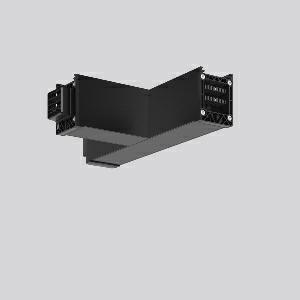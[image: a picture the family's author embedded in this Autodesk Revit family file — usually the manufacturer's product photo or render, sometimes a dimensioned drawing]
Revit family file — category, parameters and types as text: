
# Revit family: linedo_t-verbindung_982774_003_8bc5
name_source: partatom
category: Lighting Fixtures
units: mm (PartAtom-declared; Revit-internal decimal feet)

## family parameters
Cut with Voids When Loaded = No
Host = Face
Light Source = No
Part Type = Normal
Room Calculation Point = No
Round Connector Dimension = Use Diameter
Shared = No

## types (1)
- LINEDO T-Verbindung
    Apparent Load = 0 VA
    Default Elevation = 1800 mm
    Description = Series: LINEDO
T-connector, 14-pole, connection socket / plug - plug. Housing: extruded aluminium profile, powder-coated. Cover made of plastic, surface like housing. LINEDO plug system, plastic, black. Easy connection for rigid or flexible wires. 5 membrane cable entries (2 x M20 and 3 x M25). Suitable for power supply in 7-pole version. Ready prewired. Colour-coded individual cables enable easy electromechanical separation.
Colour: jet black (RAL 9005)
Length: 330 mm
Width: 204 mm
Height: 76 mm
Weight: 1070 g
    Height = 76 mm
    Lamp = 0 x
    Length = 331 mm
    Luminous efficacy = 0 lm/W
    Manufacturer = RZB
    ModVariant = No
    Model = 982774.003
    Mounting Place = Ceiling
    Mounting Type = Surface mounted
    Number of Poles = 1
    OnlyDefault = Yes
    Power Factor = 1
    Product Name = LINEDO T-Verbindung
    Product group = Surface mounted continuous line luminaire system
    ProductGroupID = 310
    Protection Class = Protection class I
    Protection Degree = Degree of protection
    RLX_Detail_Level = 1
    RLX_Emergency_Light_Flux = 0 lm
    RLX_Emergency_Type = 0
    RLX_Emergency_Type_DB = No
    RlxData = <blob elided: 20277 chars, md5=f6250ab4>
    Standby Power = 0 W
    System Light Flux = 0 lm
    System Power = 0 W
    Type Comments = Product without accessories
    Type Image = 982774.003.jpg
    URL = http://relux.com
    VarID = ---
    Voltage = 0 V
    Weight = 0.00 kg
    Width = 204 mm

## geometry (parser evidence)
native form markers: Blend x4, Sweep x11
no freeform markers — native parametric forms only
